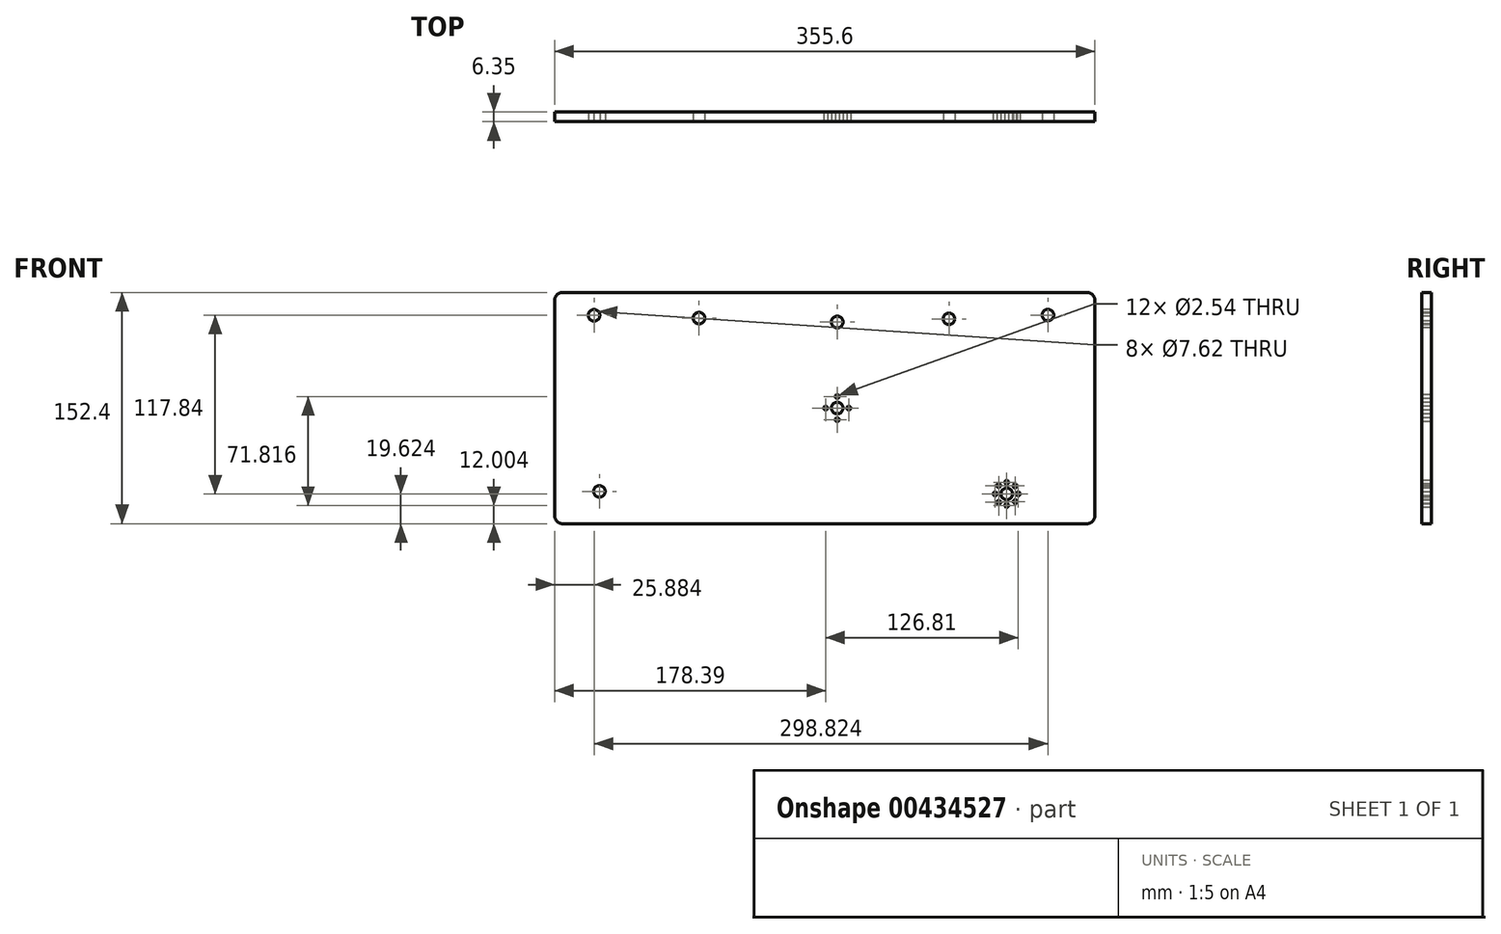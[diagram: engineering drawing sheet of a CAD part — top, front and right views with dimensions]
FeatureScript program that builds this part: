
annotation { "Feature Type Name" : "Feature", "Feature Type Description" : "" }
export const myFeature = defineFeature(function(context is Context, id is Id, definition is map)
    precondition{}
    {
        {
            var Q0;
            Q0=qCreatedBy(makeId("Front.planeOp"),FACE);
            var sketch = newSketch(context, id + "F0", { "sketchPlane" : qUnion([Q0])});
            skLineSegment(sketch, "E0.bottom", {"start": v(-186, 76.2) * mm, "end": v(169.6, 76.2) * mm});
            skLineSegment(sketch, "E0.top", {"start": v(-186, -76.2) * mm, "end": v(169.6, -76.2) * mm});
            skLineSegment(sketch, "E0.left", {"start": v(-186, 76.2) * mm, "end": v(-186, -76.2) * mm});
            skLineSegment(sketch, "E0.right", {"start": v(169.6, 76.2) * mm, "end": v(169.6, -76.2) * mm});
            skPoint(sketch, "E0.middle", {"position": v(-8.2, 0) * mm});
            skSolve(sketch);
        }
        {
            var Q0;
            Q0=qSketchRegion(id+"F0",true);
            extrude(context, id + "F1", {"entities" : qUnion([Q0]), "depth" : 6.35 * mm});
        }
        {
            var Q0;
            Q0=makeQuery(id+"F1.opExtrude","CAP_FACE",FACE,{"disambiguationData":[OSD([sQuery(id+"F0.wireOp",EDGE,"E0.bottom"),sQuery(id+"F0.wireOp",EDGE,"E0.top"),sQuery(id+"F0.wireOp",EDGE,"E0.left"),sQuery(id+"F0.wireOp",EDGE,"E0.right")])],"isStart":false});
            var sketch = newSketch(context, id + "F2", { "sketchPlane" : qUnion([Q0])});
            skCircle(sketch, "E1", {"center": v(-7.62, 0) * mm, "radius": 1.27 * mm});
            skCircle(sketch, "E2", {"center": v(0, 7.62) * mm, "radius": 1.27 * mm});
            skCircle(sketch, "E3", {"center": v(7.62, 0) * mm, "radius": 1.27 * mm});
            skCircle(sketch, "E4", {"center": v(0, -7.62) * mm, "radius": 1.27 * mm});
            skSolve(sketch);
        }
        {
            var Q0;
            Q0=sQuery(id+"F2.wireOp",VERTEX,"E1.center");
            var Q1;
            Q1=sQuery(id+"F2.wireOp",VERTEX,"E2.center");
            var Q2;
            Q2=sQuery(id+"F2.wireOp",VERTEX,"E3.center");
            var Q3;
            Q3=sQuery(id+"F2.wireOp",VERTEX,"E4.center");
            var Q4;
            Q4=makeQuery(id+"F1.opExtrude","SWEPT_BODY",BODY,{"disambiguationData":[OSD([sQuery(id+"F0.wireOp",EDGE,"E0.bottom"),sQuery(id+"F0.wireOp",EDGE,"E0.top"),sQuery(id+"F0.wireOp",EDGE,"E0.left"),sQuery(id+"F0.wireOp",EDGE,"E0.right")])]});
            hole(context, id + "F3", {"style" : HoleStyle.SIMPLE, "endStyle" : HoleEndStyle.THROUGH, "holeDiameter" : 2.54 * mm, "tappedDepth" : 12.7 * mm, "tapClearance" : 3, "locations" : qUnion([Q0, Q1, Q2, Q3]), "scope" : qUnion([Q4])});
        }
        {
            var Q0;
            Q0=makeQuery(id+"F1.opExtrude","CAP_FACE",FACE,{"disambiguationData":[OSD([sQuery(id+"F0.wireOp",EDGE,"E0.bottom"),sQuery(id+"F0.wireOp",EDGE,"E0.top"),sQuery(id+"F0.wireOp",EDGE,"E0.left"),sQuery(id+"F0.wireOp",EDGE,"E0.right")])],"isStart":false});
            var sketch = newSketch(context, id + "F4", { "sketchPlane" : qUnion([Q0])});
            skCircle(sketch, "E5", {"center": v(0, 0) * mm, "radius": 3.81 * mm});
            skCircle(sketch, "E6", {"center": v(111.57, -56.58) * mm, "radius": 3.81 * mm});
            skCircle(sketch, "E7", {"center": v(138.7, 61.26) * mm, "radius": 3.81 * mm});
            skSolve(sketch);
        }
        {
            var Q0;
            Q0=sQuery(id+"F4.wireOp",VERTEX,"E5.center");
            var Q1;
            Q1=sQuery(id+"F4.wireOp",VERTEX,"E6.center");
            var Q2;
            Q2=sQuery(id+"F4.wireOp",VERTEX,"E7.center");
            var Q3;
            Q3=makeQuery(id+"F1.opExtrude","SWEPT_BODY",BODY,{"disambiguationData":[OSD([sQuery(id+"F0.wireOp",EDGE,"E0.bottom"),sQuery(id+"F0.wireOp",EDGE,"E0.top"),sQuery(id+"F0.wireOp",EDGE,"E0.left"),sQuery(id+"F0.wireOp",EDGE,"E0.right")])]});
            hole(context, id + "F5", {"style" : HoleStyle.SIMPLE, "endStyle" : HoleEndStyle.THROUGH, "holeDiameter" : 7.62 * mm, "tappedDepth" : 12.7 * mm, "tapClearance" : 3, "locations" : qUnion([Q0, Q1, Q2]), "scope" : qUnion([Q3])});
        }
        {
            var Q0;
            Q0=makeQuery(id+"F1.opExtrude","SWEPT_EDGE",EDGE,{"disambiguationData":[OSD([sQuery(id+"F0.wireOp",EDGE,"E0.bottom"),sQuery(id+"F0.wireOp",EDGE,"E0.right")])]});
            var Q1;
            Q1=makeQuery(id+"F1.opExtrude","SWEPT_EDGE",EDGE,{"disambiguationData":[OSD([sQuery(id+"F0.wireOp",EDGE,"E0.top"),sQuery(id+"F0.wireOp",EDGE,"E0.right")])]});
            var Q2;
            Q2=makeQuery(id+"F1.opExtrude","SWEPT_EDGE",EDGE,{"disambiguationData":[OSD([sQuery(id+"F0.wireOp",EDGE,"E0.bottom"),sQuery(id+"F0.wireOp",EDGE,"E0.left")])]});
            var Q3;
            Q3=makeQuery(id+"F1.opExtrude","SWEPT_EDGE",EDGE,{"disambiguationData":[OSD([sQuery(id+"F0.wireOp",EDGE,"E0.top"),sQuery(id+"F0.wireOp",EDGE,"E0.left")])]});
            fillet(context, id + "F6", {"entities" : qUnion([Q0, Q1, Q2, Q3]), "radius" : 5.08 * mm, "tangentPropagation" : true, "allowEdgeOverflow" : false});
        }
        {
            var Q0;
            Q0=makeQuery(id+"F1.opExtrude","CAP_FACE",FACE,{"disambiguationData":[OSD([sQuery(id+"F0.wireOp",EDGE,"E0.bottom"),sQuery(id+"F0.wireOp",EDGE,"E0.top"),sQuery(id+"F0.wireOp",EDGE,"E0.left"),sQuery(id+"F0.wireOp",EDGE,"E0.right")])],"isStart":false});
            var sketch = newSketch(context, id + "F7", { "sketchPlane" : qUnion([Q0])});
            skCircle(sketch, "E8", {"center": v(111.57, -48.96) * mm, "radius": 1.27 * mm});
            skCircle(sketch, "E9", {"center": v(119.2, -56.58) * mm, "radius": 1.27 * mm});
            skCircle(sketch, "E10", {"center": v(103.95, -56.58) * mm, "radius": 1.27 * mm});
            skCircle(sketch, "E11", {"center": v(111.57, -64.2) * mm, "radius": 1.27 * mm});
            skPoint(sketch, "E12.orphan", {"position": v(111.57, -56.58) * mm});
            skCircle(sketch, "E13", {"center": v(106.33, -51.05) * mm, "radius": 1.27 * mm});
            skCircle(sketch, "E14", {"center": v(117.05, -51.28) * mm, "radius": 1.27 * mm});
            skCircle(sketch, "E15", {"center": v(117.24, -61.67) * mm, "radius": 1.27 * mm});
            skCircle(sketch, "E16", {"center": v(106.34, -62.12) * mm, "radius": 1.27 * mm});
            skSolve(sketch);
        }
        {
            var Q0;
            Q0=sQuery(id+"F7.wireOp",VERTEX,"E8.center");
            var Q1;
            Q1=sQuery(id+"F7.wireOp",VERTEX,"E14.center");
            var Q2;
            Q2=sQuery(id+"F7.wireOp",VERTEX,"E9.center");
            var Q3;
            Q3=sQuery(id+"F7.wireOp",VERTEX,"E15.center");
            var Q4;
            Q4=sQuery(id+"F7.wireOp",VERTEX,"E11.center");
            var Q5;
            Q5=sQuery(id+"F7.wireOp",VERTEX,"E16.center");
            var Q6;
            Q6=sQuery(id+"F7.wireOp",VERTEX,"E10.center");
            var Q7;
            Q7=sQuery(id+"F7.wireOp",VERTEX,"E13.center");
            var Q8;
            Q8=makeQuery(id+"F1.opExtrude","SWEPT_BODY",BODY,{"disambiguationData":[OSD([sQuery(id+"F0.wireOp",EDGE,"E0.bottom"),sQuery(id+"F0.wireOp",EDGE,"E0.top"),sQuery(id+"F0.wireOp",EDGE,"E0.left"),sQuery(id+"F0.wireOp",EDGE,"E0.right")])]});
            hole(context, id + "F8", {"style" : HoleStyle.SIMPLE, "endStyle" : HoleEndStyle.THROUGH, "holeDiameter" : 2.54 * mm, "tappedDepth" : 12.7 * mm, "tapClearance" : 3, "locations" : qUnion([Q0, Q1, Q2, Q3, Q4, Q5, Q6, Q7]), "scope" : qUnion([Q8])});
        }
        {
            var Q0;
            Q0=makeQuery(id+"F1.opExtrude","CAP_FACE",FACE,{"disambiguationData":[OSD([sQuery(id+"F0.wireOp",EDGE,"E0.bottom"),sQuery(id+"F0.wireOp",EDGE,"E0.top"),sQuery(id+"F0.wireOp",EDGE,"E0.left"),sQuery(id+"F0.wireOp",EDGE,"E0.right")])],"isStart":false});
            var sketch = newSketch(context, id + "F9", { "sketchPlane" : qUnion([Q0])});
            skCircle(sketch, "E17", {"center": v(-156.6, -54.9) * mm, "radius": 3.81 * mm});
            skSolve(sketch);
        }
        {
            var Q0;
            Q0=sQuery(id+"F9.wireOp",VERTEX,"E17.center");
            var Q1;
            Q1=makeQuery(id+"F1.opExtrude","SWEPT_BODY",BODY,{"disambiguationData":[OSD([sQuery(id+"F0.wireOp",EDGE,"E0.bottom"),sQuery(id+"F0.wireOp",EDGE,"E0.top"),sQuery(id+"F0.wireOp",EDGE,"E0.left"),sQuery(id+"F0.wireOp",EDGE,"E0.right")])]});
            hole(context, id + "F10", {"style" : HoleStyle.SIMPLE, "endStyle" : HoleEndStyle.THROUGH, "holeDiameter" : 7.62 * mm, "isTappedThrough" : true, "tappedDepth" : 12.7 * mm, "tapClearance" : 3, "locations" : qUnion([Q0]), "scope" : qUnion([Q1])});
        }
        {
            var Q0;
            Q0=makeQuery(id+"F1.opExtrude","CAP_FACE",FACE,{"disambiguationData":[OSD([sQuery(id+"F0.wireOp",EDGE,"E0.bottom"),sQuery(id+"F0.wireOp",EDGE,"E0.top"),sQuery(id+"F0.wireOp",EDGE,"E0.left"),sQuery(id+"F0.wireOp",EDGE,"E0.right")])],"isStart":false});
            var sketch = newSketch(context, id + "F11", { "sketchPlane" : qUnion([Q0])});
            skCircle(sketch, "E18", {"center": v(73.53, 58.8) * mm, "radius": 3.81 * mm});
            skCircle(sketch, "E19", {"center": v(-160.13, 61.16) * mm, "radius": 3.81 * mm});
            skSolve(sketch);
        }
        {
            var Q0;
            Q0=sQuery(id+"F11.wireOp",VERTEX,"E18.center");
            var Q1;
            Q1=sQuery(id+"F11.wireOp",VERTEX,"E19.center");
            var Q2;
            Q2=makeQuery(id+"F1.opExtrude","SWEPT_BODY",BODY,{"disambiguationData":[OSD([sQuery(id+"F0.wireOp",EDGE,"E0.bottom"),sQuery(id+"F0.wireOp",EDGE,"E0.top"),sQuery(id+"F0.wireOp",EDGE,"E0.left"),sQuery(id+"F0.wireOp",EDGE,"E0.right")])]});
            hole(context, id + "F12", {"style" : HoleStyle.SIMPLE, "endStyle" : HoleEndStyle.THROUGH, "holeDiameter" : 7.62 * mm, "isTappedThrough" : true, "tappedDepth" : 12.7 * mm, "tapClearance" : 3, "locations" : qUnion([Q0, Q1]), "scope" : qUnion([Q2])});
        }
        {
            var Q0;
            Q0=makeQuery(id+"F1.opExtrude","CAP_FACE",FACE,{"disambiguationData":[OSD([sQuery(id+"F0.wireOp",EDGE,"E0.bottom"),sQuery(id+"F0.wireOp",EDGE,"E0.top"),sQuery(id+"F0.wireOp",EDGE,"E0.left"),sQuery(id+"F0.wireOp",EDGE,"E0.right")])],"isStart":false});
            var sketch = newSketch(context, id + "F13", { "sketchPlane" : qUnion([Q0])});
            skCircle(sketch, "E20", {"center": v(-91.05, 59.28) * mm, "radius": 3.81 * mm});
            skSolve(sketch);
        }
        {
            var Q0;
            Q0=sQuery(id+"F13.wireOp",VERTEX,"E20.center");
            var Q1;
            Q1=makeQuery(id+"F1.opExtrude","SWEPT_BODY",BODY,{"disambiguationData":[OSD([sQuery(id+"F0.wireOp",EDGE,"E0.bottom"),sQuery(id+"F0.wireOp",EDGE,"E0.top"),sQuery(id+"F0.wireOp",EDGE,"E0.left"),sQuery(id+"F0.wireOp",EDGE,"E0.right")])]});
            hole(context, id + "F14", {"style" : HoleStyle.SIMPLE, "endStyle" : HoleEndStyle.THROUGH, "holeDiameter" : 7.62 * mm, "isTappedThrough" : true, "tappedDepth" : 12.7 * mm, "tapClearance" : 3, "locations" : qUnion([Q0]), "scope" : qUnion([Q1])});
        }
        {
            var Q0;
            Q0=makeQuery(id+"F1.opExtrude","CAP_FACE",FACE,{"disambiguationData":[OSD([sQuery(id+"F0.wireOp",EDGE,"E0.bottom"),sQuery(id+"F0.wireOp",EDGE,"E0.top"),sQuery(id+"F0.wireOp",EDGE,"E0.left"),sQuery(id+"F0.wireOp",EDGE,"E0.right")])],"isStart":false});
            var sketch = newSketch(context, id + "F15", { "sketchPlane" : qUnion([Q0])});
            skCircle(sketch, "E21", {"center": v(0, 56.72) * mm, "radius": 3.81 * mm});
            skSolve(sketch);
        }
        {
            var Q0;
            Q0=sQuery(id+"F15.wireOp",VERTEX,"E21.center");
            var Q1;
            Q1=makeQuery(id+"F1.opExtrude","SWEPT_BODY",BODY,{"disambiguationData":[OSD([sQuery(id+"F0.wireOp",EDGE,"E0.bottom"),sQuery(id+"F0.wireOp",EDGE,"E0.top"),sQuery(id+"F0.wireOp",EDGE,"E0.left"),sQuery(id+"F0.wireOp",EDGE,"E0.right")])]});
            hole(context, id + "F16", {"style" : HoleStyle.SIMPLE, "endStyle" : HoleEndStyle.THROUGH, "holeDiameter" : 7.62 * mm, "isTappedThrough" : true, "tappedDepth" : 12.7 * mm, "tapClearance" : 3, "locations" : qUnion([Q0]), "scope" : qUnion([Q1])});
        }
    });
